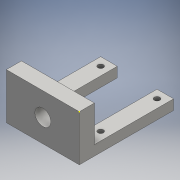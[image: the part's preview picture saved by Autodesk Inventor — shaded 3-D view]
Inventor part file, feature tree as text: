
AUTODESK INVENTOR PART (.ipt)
format: ipt  version: 2016 (Build 200138000, 138)  size: 128,512 bytes
history: native  units: mm
features: sketch x6, extrude x3, hole x2
ambient origin geometry x8: Origin, YZ Plane, XZ Plane, XY Plane, X Axis, Y Axis, Z Axis, Center Point
bodies: Solid1 (feature_tree)
feature tree (11):
  extrude  "Extrusion1"  Depth=18.3mm
  extrude  "Extrusion2"  Depth=6.6mm
  extrude  "Extrusion3"  Depth=31.5mm TaperAngle=0.0deg
  hole  "Hole1"  [1 undecoded]
  sketch  "Sketch5"  dims[d10=31.5mm d11=0.0mm d14=5.8mm]
  hole  "Hole2"  [1 undecoded]
  sketch  "Sketch1"  dims[d0=29.0mm d1=18.3mm]
  sketch  "Sketch2"  dims[d2=6.0mm d3=0.0mm d4=6.6mm]
  sketch  "Sketch3"  dims[d5=4.0mm d6=31.5mm d7=0.0mm]
  sketch  "Sketch4"  dims[d8=6.6mm d9=4.0mm]
  sketch  "Sketch6"  dims[d15=22.4mm d16=22.4mm d17=22.4mm d18=5.8mm d19=2.2mm d20=6.0mm d21=4.0mm d22=2.0mm d23=90.0deg d24=8.0mm d25=20.594885mm d26=9.15mm d27=6.35mm d28=6.0mm d29=4.0mm d30=2.0mm d31=90.0deg d32=8.0mm d33=20.594885mm]
note: 2 required parameter values undecoded (feature->parameter linkage not recoverable at this tier; creation-order binding heuristic only, values carry confidence <= 0.55)
